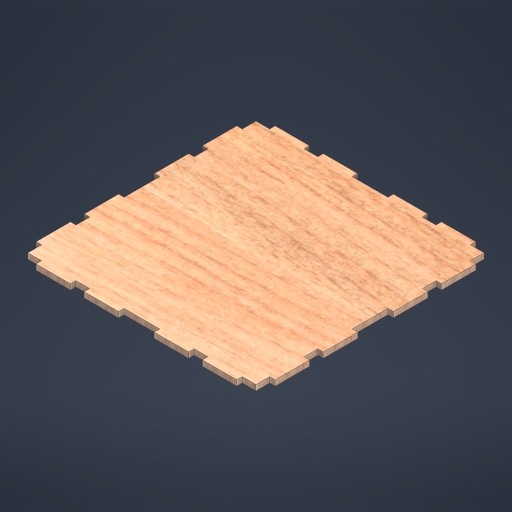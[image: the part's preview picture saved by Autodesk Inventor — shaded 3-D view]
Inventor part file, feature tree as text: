
AUTODESK INVENTOR PART (.ipt)
format: ipt  version: 2024.1 (Build 281209000, 209)  size: 487,936 bytes
history: native  units: mm
features: extrude x1, sketch x1
ambient origin geometry x8: Origin, YZ Plane, XZ Plane, XY Plane, X Axis, Y Axis, Z Axis, Center Point
bodies: Solid1 (feature_tree)
feature tree (2):
  extrude  "Extrusion1"  Depth=100.0mm
  sketch  "Sketch1"  dims[d0=12.0mm d1=100.0mm d3=16.0mm d4=100.0mm d6=16.0mm d9=5.0mm d10=5.0mm d11=4.0mm d12=4.0mm d13=10.0mm d14=10.0mm d15=25.0mm d16=4.0mm d17=25.0mm d18=10.0mm d19=25.0mm d20=10.0mm d21=25.0mm d22=4.0mm d23=40.0mm d25=360.0deg d27=4.0mm d28=0.0mm]
